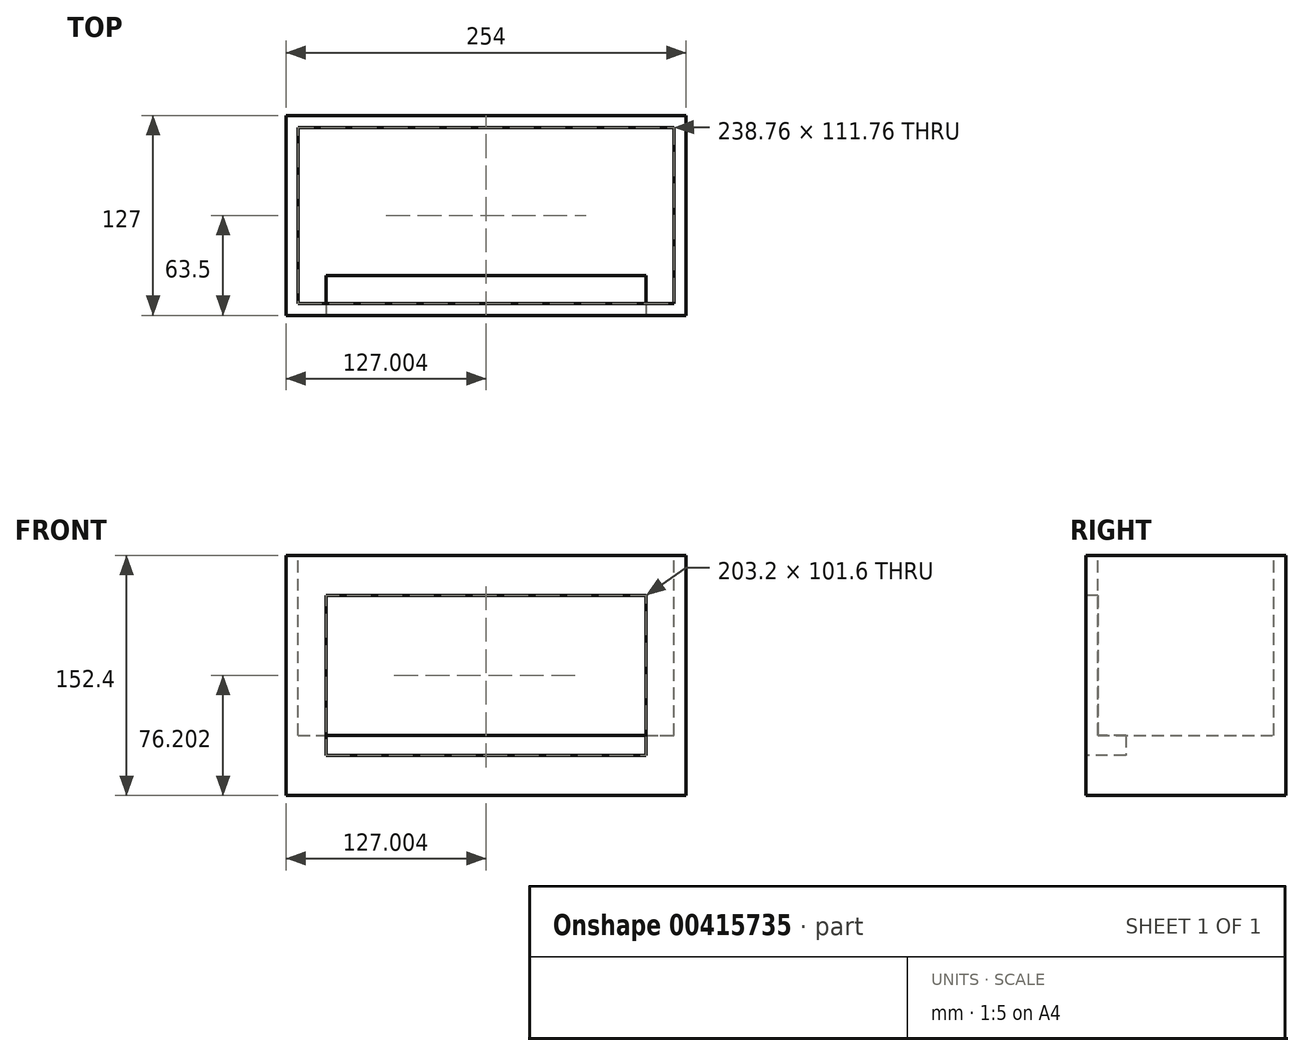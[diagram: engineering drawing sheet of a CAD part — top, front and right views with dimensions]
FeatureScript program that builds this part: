
annotation { "Feature Type Name" : "Feature", "Feature Type Description" : "" }
export const myFeature = defineFeature(function(context is Context, id is Id, definition is map)
    precondition{}
    {
        {
            var Q0;
            Q0=qCreatedBy(makeId("Front.planeOp"),FACE);
            var sketch = newSketch(context, id + "F0", { "sketchPlane" : qUnion([Q0])});
            skLineSegment(sketch, "E0.bottom", {"start": v(-117.39, 92.05) * mm, "end": v(136.61, 92.05) * mm});
            skLineSegment(sketch, "E0.top", {"start": v(-117.39, -60.35) * mm, "end": v(136.61, -60.35) * mm});
            skLineSegment(sketch, "E0.left", {"start": v(-117.39, 92.05) * mm, "end": v(-117.39, -60.35) * mm});
            skLineSegment(sketch, "E0.right", {"start": v(136.61, 92.05) * mm, "end": v(136.61, -60.35) * mm});
            skSolve(sketch);
        }
        {
            var Q0;
            Q0 = qSketchRegion(id + "F0", true);
            extrude(context, id + "F1", {"entities" : qUnion([Q0]), "endBound" : BoundingType.SYMMETRIC, "depth" : 127 * mm});
        }
        {
            var Q0;
            Q0=makeQuery(id+"F1.opExtrude","SWEPT_FACE",FACE,{"disambiguationData":[OSD([sQuery(id+"F0.wireOp",EDGE,"E0.bottom")])]});
            var sketch = newSketch(context, id + "F2", { "sketchPlane" : qUnion([Q0])});
            skLineSegment(sketch, "E1.bottom", {"start": v(-109.77, -55.88) * mm, "end": v(129, -55.88) * mm});
            skLineSegment(sketch, "E1.top", {"start": v(-109.77, 55.88) * mm, "end": v(129, 55.88) * mm});
            skLineSegment(sketch, "E1.left", {"start": v(-109.77, -55.88) * mm, "end": v(-109.77, 55.88) * mm});
            skLineSegment(sketch, "E1.right", {"start": v(129, -55.88) * mm, "end": v(129, 55.88) * mm});
            skSolve(sketch);
        }
        {
            var Q0;
            Q0=makeQuery(id+"F2.imprint","IMPRINT",FACE,{"disambiguationData":[TD([[makeQuery(id+"F2.imprint","IMPRINT",EDGE,{"derivedFrom":sQuery(id+"F2.wireOp",EDGE,"E1.bottom")}),1.0]])]});
            extrude(context, id + "F3", {"entities" : qUnion([Q0]), "operationType" : NewBodyOperationType.REMOVE, "oppositeDirection" : true, "depth" : 114.3 * mm});
        }
        {
            var Q0;
            Q0=makeQuery(id+"F1.opExtrude","CAP_FACE",FACE,{"disambiguationData":[OSD([sQuery(id+"F0.wireOp",EDGE,"E0.bottom"),sQuery(id+"F0.wireOp",EDGE,"E0.top"),sQuery(id+"F0.wireOp",EDGE,"E0.left"),sQuery(id+"F0.wireOp",EDGE,"E0.right")])],"isStart":false});
            var sketch = newSketch(context, id + "F4", { "sketchPlane" : qUnion([Q0])});
            skLineSegment(sketch, "E2.bottom", {"start": v(-91.99, 66.65) * mm, "end": v(111.21, 66.65) * mm});
            skLineSegment(sketch, "E2.top", {"start": v(-91.99, -34.95) * mm, "end": v(111.21, -34.95) * mm});
            skLineSegment(sketch, "E2.left", {"start": v(-91.99, 66.65) * mm, "end": v(-91.99, -34.95) * mm});
            skLineSegment(sketch, "E2.right", {"start": v(111.21, 66.65) * mm, "end": v(111.21, -34.95) * mm});
            skSolve(sketch);
        }
        {
            var Q0;
            Q0=makeQuery(id+"F4.imprint","IMPRINT",FACE,{"disambiguationData":[TD([[makeQuery(id+"F4.imprint","IMPRINT",EDGE,{"derivedFrom":sQuery(id+"F4.wireOp",EDGE,"E2.bottom")}),-1.0]])]});
            extrude(context, id + "F5", {"entities" : qUnion([Q0]), "operationType" : NewBodyOperationType.REMOVE, "oppositeDirection" : true, "depth" : 25.4 * mm});
        }
    });
